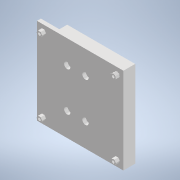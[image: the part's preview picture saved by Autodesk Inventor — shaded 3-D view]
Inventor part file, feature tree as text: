
AUTODESK INVENTOR PART (.ipt)
format: ipt  version: 2020 (Build 240168000, 168)  size: 282,112 bytes
history: native  units: mm
features: reference x12, other x10, sketch x8, extrude x6, projected_geometry x4, hole x2
ambient origin geometry x8: Origin, YZ Plane, XZ Plane, XY Plane, X Axis, Y Axis, Z Axis, Center Point
bodies: Body1 (feature_tree)
feature tree (42):
  other  "솔리드1"
  extrude  "돌출1"  Depth=110.0mm
  sketch  "스케치2"
  other  "작업 평면1"
  extrude  "돌출2"  Depth=110.0mm
  extrude  "돌출3"  Depth=15.0mm TaperAngle=0.0deg
  hole  "구멍1"  [1 undecoded]
  extrude  "돌출4"  Depth=5.0mm
  extrude  "돌출5"  Depth=15.0mm TaperAngle=0.0deg
  extrude  "돌출6"  Depth=8.0mm
  hole  "구멍2"  [1 undecoded]
  sketch  "스케치1"
  reference  "참조1"
  reference  "참조2"
  reference  "참조3"
  reference  "참조4"
  reference  "참조5"
  reference  "참조6"
  reference  "참조7"
  reference  "참조8"
  sketch  "스케치3"
  reference  "참조9"
  sketch  "스케치4"
  reference  "참조10"
  reference  "참조11"
  reference  "참조12"
  sketch  "스케치7"
  sketch  "스케치9"
  projected_geometry  "투영된 루프2"
  sketch  "스케치10"
  projected_geometry  "투영된 루프3"
  projected_geometry  "투영된 루프4"
  sketch  "스케치11"
  projected_geometry  "투영된 루프5"
  parser-record x1  (decoder bookkeeping rows leaked as tree rows — omitted from the tree; the rows remain in map.json)
  other  "v6.iam"
  other  "bumper_final_1:1"
  other  "bumper_final_5:1"
  other  "AL_profile_final:2"
  other  "AL_profile_final:1"
  other  "horiz_bar:2"
  other  "bumper_final_6:1"
note: 2 required parameter values undecoded (feature->parameter linkage not recoverable at this tier; creation-order binding heuristic only, values carry confidence <= 0.55)
note: 1 file-system path scrubbed to <path> (originals preserved in map.json)
